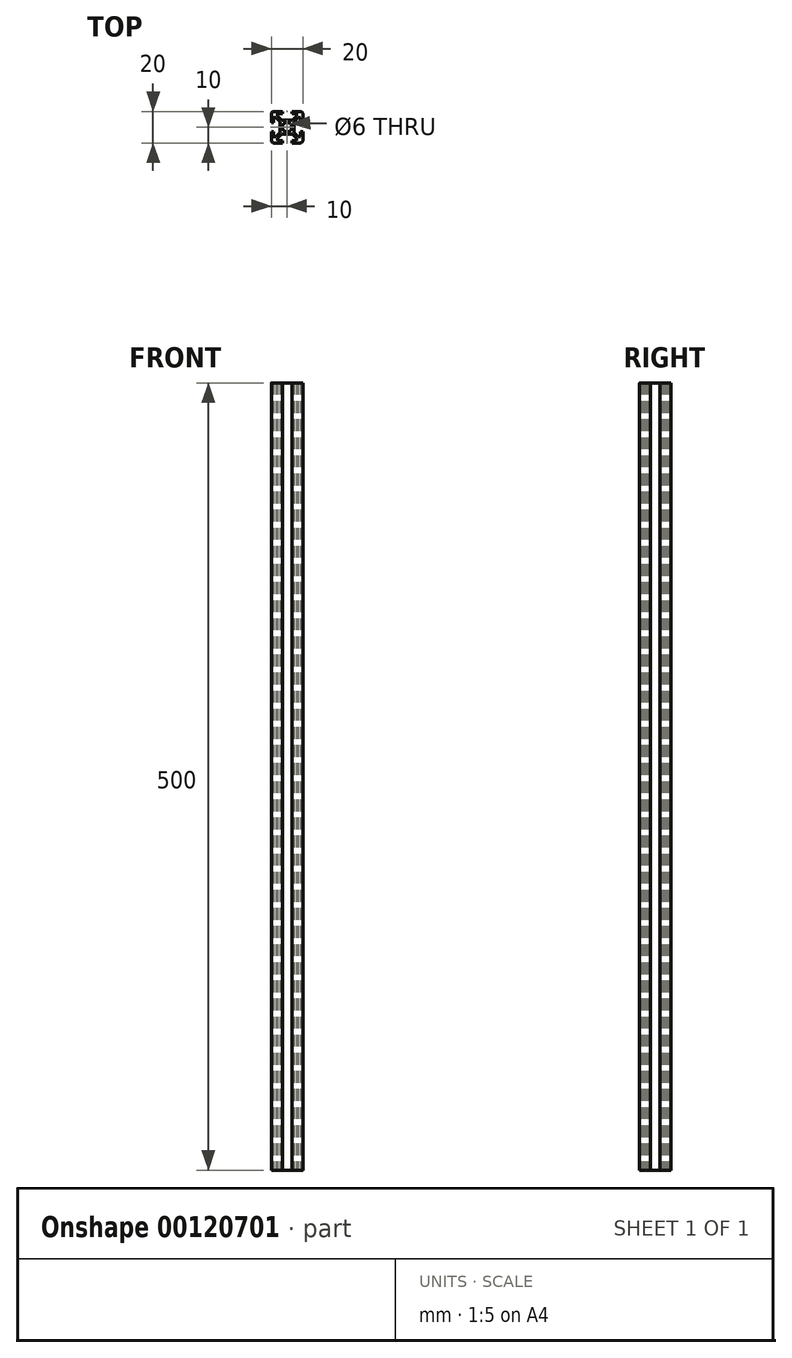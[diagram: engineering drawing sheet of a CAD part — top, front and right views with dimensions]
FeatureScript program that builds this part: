
annotation { "Feature Type Name" : "Feature", "Feature Type Description" : "" }
export const myFeature = defineFeature(function(context is Context, id is Id, definition is map)
    precondition{}
    {
        {
            var Q0;
            Q0=qCreatedBy(makeId("Top.planeOp"),FACE);
            var sketch = newSketch(context, id + "F0", { "sketchPlane" : qUnion([Q0])});
            skLineSegment(sketch, "E0.bottom", {"start": v(1.5, 0) * mm, "end": v(7, 0) * mm});
            skLineSegment(sketch, "E0.top", {"start": v(1.5, 20) * mm, "end": v(7, 20) * mm});
            skLineSegment(sketch, "E0.left", {"start": v(0, 1.5) * mm, "end": v(0, 7) * mm});
            skLineSegment(sketch, "E0.right", {"start": v(20, 1.5) * mm, "end": v(20, 7) * mm});
            skLineSegment(sketch, "E1", {"start": v(10, 25.59) * mm, "end": v(10, -6.26) * mm, "construction": true});
            skPoint(sketch, "E1.startSnap0", {"position": v(10, 20) * mm});
            skLineSegment(sketch, "E2", {"start": v(-5.38, 10) * mm, "end": v(26.16, 10) * mm, "construction": true});
            skPoint(sketch, "E2.startSnap0", {"position": v(0, 10) * mm});
            skPoint(sketch, "E3.visualSharp", {"position": v(20, 20) * mm});
            skArc(sketch, "E3.filletArc", {"start": v(20, 18.5) * mm, "mid": v(19.56, 19.56) * mm, "end": v(18.5, 20) * mm});
            skPoint(sketch, "E4.visualSharp", {"position": v(20, 0) * mm});
            skArc(sketch, "E4.filletArc", {"start": v(18.5, 0) * mm, "mid": v(19.56, 0.44) * mm, "end": v(20, 1.5) * mm});
            skPoint(sketch, "E5.visualSharp", {"position": v(0, 0) * mm});
            skArc(sketch, "E5.filletArc", {"start": v(0, 1.5) * mm, "mid": v(0.44, 0.44) * mm, "end": v(1.5, 0) * mm});
            skPoint(sketch, "E6.visualSharp", {"position": v(0, 20) * mm});
            skArc(sketch, "E6.filletArc", {"start": v(1.5, 20) * mm, "mid": v(0.44, 19.56) * mm, "end": v(0, 18.5) * mm});
            skLineSegment(sketch, "E7", {"start": v(20, 13) * mm, "end": v(18.5, 13) * mm});
            skLineSegment(sketch, "E8", {"start": v(18.5, 13) * mm, "end": v(18.5, 16) * mm});
            skLineSegment(sketch, "E9", {"start": v(18.5, 16) * mm, "end": v(17, 16) * mm});
            skLineSegment(sketch, "E10", {"start": v(17, 16) * mm, "end": v(14.5, 13.5) * mm});
            skLineSegment(sketch, "E11", {"start": v(14.5, 13.5) * mm, "end": v(14.5, 10) * mm});
            skLineSegment(sketch, "E12.MirrorCS", {"start": v(20, 7) * mm, "end": v(18.5, 7) * mm});
            skLineSegment(sketch, "E13.MirrorCS", {"start": v(18.5, 7) * mm, "end": v(18.5, 4) * mm});
            skLineSegment(sketch, "E14.MirrorCS", {"start": v(18.5, 4) * mm, "end": v(17, 4) * mm});
            skLineSegment(sketch, "E15.MirrorCS", {"start": v(14.5, 6.5) * mm, "end": v(14.5, 10) * mm});
            skLineSegment(sketch, "E16.MirrorCS", {"start": v(17, 4) * mm, "end": v(14.5, 6.5) * mm});
            skLineSegment(sketch, "E17.MirrorCS", {"start": v(0, 13) * mm, "end": v(1.5, 13) * mm});
            skLineSegment(sketch, "E18.MirrorCS", {"start": v(1.5, 13) * mm, "end": v(1.5, 16) * mm});
            skLineSegment(sketch, "E19.MirrorCS", {"start": v(1.5, 16) * mm, "end": v(3, 16) * mm});
            skLineSegment(sketch, "E20.MirrorCS", {"start": v(3, 16) * mm, "end": v(5.5, 13.5) * mm});
            skLineSegment(sketch, "E21.MirrorCS", {"start": v(5.5, 13.5) * mm, "end": v(5.5, 10) * mm});
            skLineSegment(sketch, "E22.MirrorCS", {"start": v(5.5, 6.5) * mm, "end": v(5.5, 10) * mm});
            skLineSegment(sketch, "E23.MirrorCS", {"start": v(3, 4) * mm, "end": v(5.5, 6.5) * mm});
            skLineSegment(sketch, "E24.MirrorCS", {"start": v(1.5, 4) * mm, "end": v(3, 4) * mm});
            skLineSegment(sketch, "E25.MirrorCS", {"start": v(1.5, 7) * mm, "end": v(1.5, 4) * mm});
            skLineSegment(sketch, "E26.MirrorCS", {"start": v(0, 7) * mm, "end": v(1.5, 7) * mm});
            skLineSegment(sketch, "E27.1.0", {"start": v(13, 20) * mm, "end": v(13, 18.5) * mm});
            skLineSegment(sketch, "E27.1.1", {"start": v(13, 18.5) * mm, "end": v(16, 18.5) * mm});
            skLineSegment(sketch, "E27.1.2", {"start": v(16, 18.5) * mm, "end": v(16, 17) * mm});
            skLineSegment(sketch, "E27.1.3", {"start": v(16, 17) * mm, "end": v(13.5, 14.5) * mm});
            skLineSegment(sketch, "E27.1.4", {"start": v(13.5, 14.5) * mm, "end": v(10, 14.5) * mm});
            skLineSegment(sketch, "E27.1.5", {"start": v(6.5, 14.5) * mm, "end": v(10, 14.5) * mm});
            skLineSegment(sketch, "E27.1.6", {"start": v(4, 17) * mm, "end": v(6.5, 14.5) * mm});
            skLineSegment(sketch, "E27.1.7", {"start": v(4, 18.5) * mm, "end": v(4, 17) * mm});
            skLineSegment(sketch, "E27.1.8", {"start": v(7, 18.5) * mm, "end": v(4, 18.5) * mm});
            skLineSegment(sketch, "E27.1.9", {"start": v(7, 20) * mm, "end": v(7, 18.5) * mm});
            skPoint(sketch, "E27.center", {"position": v(10, 10) * mm});
            skLineSegment(sketch, "E27.anchor1", {"start": v(10, 10) * mm, "end": v(0, 13) * mm, "construction": true});
            skLineSegment(sketch, "E27.anchor2", {"start": v(10, 10) * mm, "end": v(13, 20) * mm, "construction": true});
            skLineSegment(sketch, "E28.MirrorCS", {"start": v(7, 0) * mm, "end": v(7, 1.5) * mm});
            skLineSegment(sketch, "E29.MirrorCS", {"start": v(7, 1.5) * mm, "end": v(4, 1.5) * mm});
            skLineSegment(sketch, "E30.MirrorCS", {"start": v(4, 1.5) * mm, "end": v(4, 3) * mm});
            skLineSegment(sketch, "E31.MirrorCS", {"start": v(4, 3) * mm, "end": v(6.5, 5.5) * mm});
            skLineSegment(sketch, "E32.MirrorCS", {"start": v(6.5, 5.5) * mm, "end": v(10, 5.5) * mm});
            skLineSegment(sketch, "E33.MirrorCS", {"start": v(13.5, 5.5) * mm, "end": v(10, 5.5) * mm});
            skLineSegment(sketch, "E34.MirrorCS", {"start": v(16, 3) * mm, "end": v(13.5, 5.5) * mm});
            skLineSegment(sketch, "E35.MirrorCS", {"start": v(16, 1.5) * mm, "end": v(16, 3) * mm});
            skLineSegment(sketch, "E36.MirrorCS", {"start": v(13, 1.5) * mm, "end": v(16, 1.5) * mm});
            skLineSegment(sketch, "E37.MirrorCS", {"start": v(13, 0) * mm, "end": v(13, 1.5) * mm});
            skLineSegment(sketch, "E38.trimOffspring", {"start": v(13, 20) * mm, "end": v(18.5, 20) * mm});
            skLineSegment(sketch, "E39.trimOffspring", {"start": v(20, 13) * mm, "end": v(20, 18.5) * mm});
            skLineSegment(sketch, "E40.trimOffspring", {"start": v(13, 0) * mm, "end": v(18.5, 0) * mm});
            skLineSegment(sketch, "E41.trimOffspring", {"start": v(0, 13) * mm, "end": v(0, 18.5) * mm});
            skCircle(sketch, "E42", {"center": v(10, 10) * mm, "radius": 3 * mm});
            skSolve(sketch);
        }
        {
            var Q0;
            Q0 = qSketchRegion(id + "F0", true);
            extrude(context, id + "F1", {"entities" : qUnion([Q0]), "depth" : 500 * mm});
        }
    });
